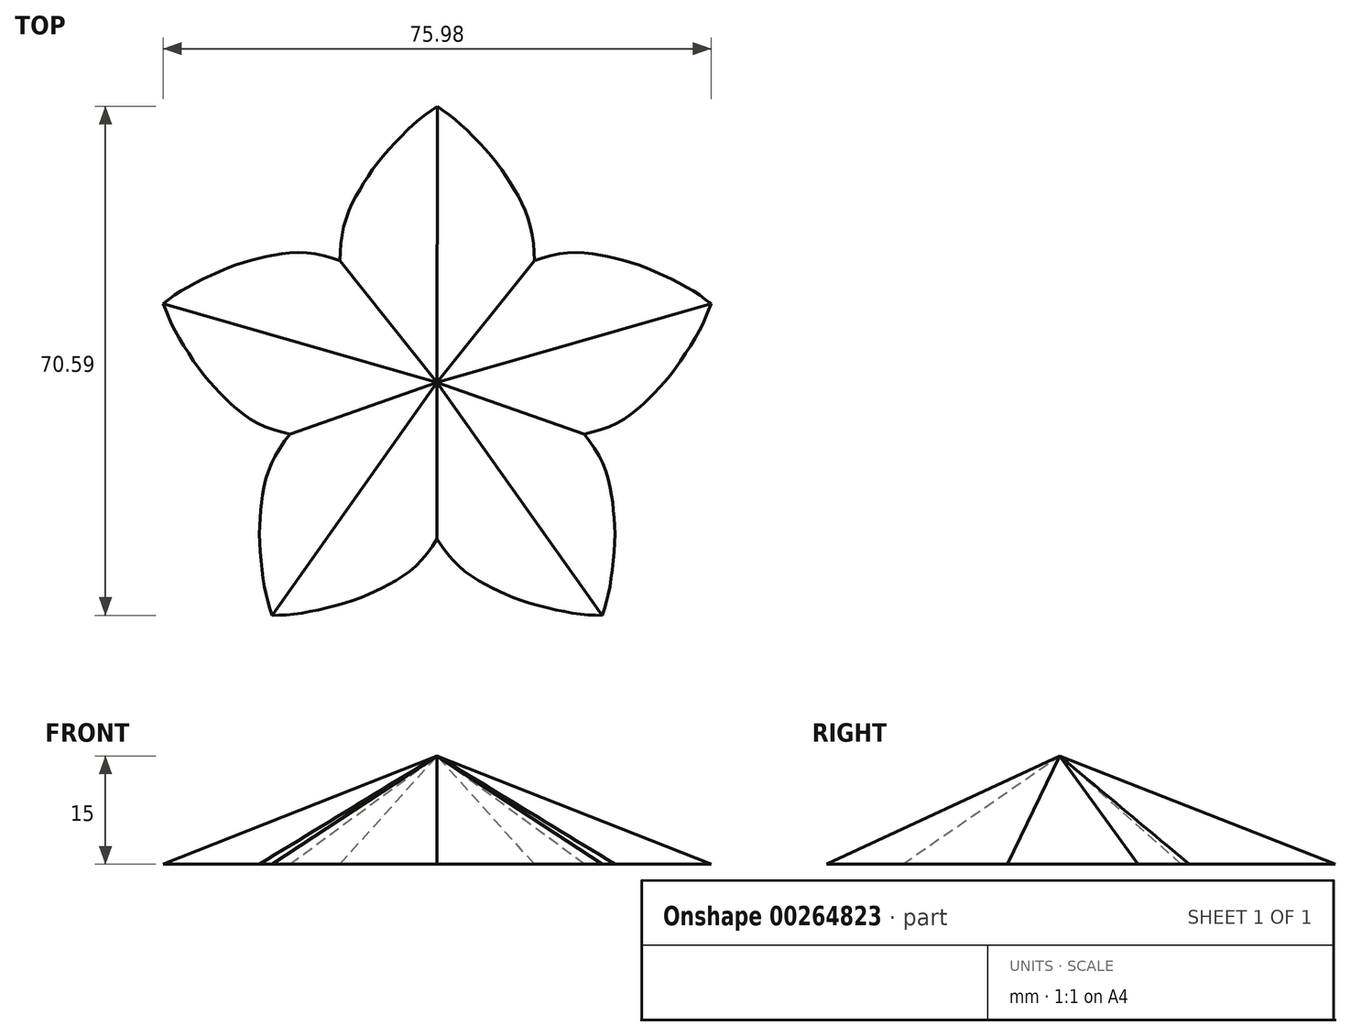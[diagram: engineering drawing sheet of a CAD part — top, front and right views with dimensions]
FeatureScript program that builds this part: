
annotation { "Feature Type Name" : "Feature", "Feature Type Description" : "" }
export const myFeature = defineFeature(function(context is Context, id is Id, definition is map)
    precondition{}
    {
        {
            var Q0;
            Q0=qCreatedBy(makeId("Top.planeOp"),FACE);
            var sketch = newSketch(context, id + "F0", { "sketchPlane" : qUnion([Q0])});
            skFitSpline(sketch, "E0", {"points": [v(-0.02, -18.8) * mm, v(2.46, -22.06) * mm, v(5.56, -24.49) * mm, v(8.5, -26.02) * mm, v(11.82, -27.4) * mm, v(16.13, -28.56) * mm, v(19.98, -29.26) * mm, v(22.9, -29.4) * mm], "startDerivative": vector(15.3, -22.9) * mm, "endDerivative": vector(22.31, -0.58) * mm});
            skFitSpline(sketch, "E1.MirrorCS", {"points": [v(0, -18.8) * mm, v(-2.46, -22.06) * mm, v(-5.56, -24.49) * mm, v(-8.5, -26.02) * mm, v(-11.82, -27.4) * mm, v(-16.13, -28.56) * mm, v(-19.98, -29.26) * mm, v(-22.9, -29.4) * mm], "startDerivative": vector(-15.3, -22.9) * mm, "endDerivative": vector(-22.31, -0.58) * mm});
            skFitSpline(sketch, "E2.MirrorCS", {"points": [v(-20.43, -4.3) * mm, v(-22.7, -7.7) * mm, v(-23.96, -11.42) * mm, v(-24.44, -14.7) * mm, v(-24.64, -18.3) * mm, v(-24.32, -22.75) * mm, v(-23.71, -26.6) * mm, v(-22.9, -29.4) * mm], "startDerivative": vector(-16.57, -22) * mm, "endDerivative": vector(6.8, -21.26) * mm});
            skFitSpline(sketch, "E3.MirrorCS", {"points": [v(20.43, -4.3) * mm, v(22.7, -7.7) * mm, v(23.96, -11.42) * mm, v(24.44, -14.7) * mm, v(24.64, -18.3) * mm, v(24.32, -22.75) * mm, v(23.71, -26.6) * mm, v(22.9, -29.4) * mm], "startDerivative": vector(16.57, -22) * mm, "endDerivative": vector(-6.8, -21.26) * mm});
            skFitSpline(sketch, "E4.MirrorCS", {"points": [v(-20.43, -4.3) * mm, v(-24.31, -3.05) * mm, v(-27.63, -0.92) * mm, v(-30.05, 1.35) * mm, v(-32.44, 4.03) * mm, v(-34.96, 7.72) * mm, v(-36.88, 11.12) * mm, v(-37.99, 13.82) * mm], "startDerivative": vector(-26.66, 6.9) * mm, "endDerivative": vector(-7.9, 20.87) * mm});
            skFitSpline(sketch, "E5.MirrorCS", {"points": [v(-13.48, 19.78) * mm, v(-17.42, 20.79) * mm, v(-21.36, 20.76) * mm, v(-24.62, 20.12) * mm, v(-28.07, 19.14) * mm, v(-32.17, 17.36) * mm, v(-35.61, 15.51) * mm, v(-37.99, 13.82) * mm], "startDerivative": vector(-26.23, 8.4) * mm, "endDerivative": vector(-17.83, -13.43) * mm});
            skFitSpline(sketch, "E6.MirrorCS", {"points": [v(20.43, -4.3) * mm, v(24.31, -3.05) * mm, v(27.63, -0.92) * mm, v(30.05, 1.35) * mm, v(32.44, 4.03) * mm, v(34.96, 7.72) * mm, v(36.88, 11.12) * mm, v(37.99, 13.82) * mm], "startDerivative": vector(26.66, 6.9) * mm, "endDerivative": vector(7.9, 20.87) * mm});
            skFitSpline(sketch, "E7.MirrorCS", {"points": [v(-13.48, 19.78) * mm, v(-13.1, 23.87) * mm, v(-11.83, 27.6) * mm, v(-10.2, 30.49) * mm, v(-8.18, 33.45) * mm, v(-5.2, 36.79) * mm, v(-2.37, 39.47) * mm, v(0.04, 41.2) * mm], "startDerivative": vector(0.3, 27.54) * mm, "endDerivative": vector(18.36, 12.69) * mm});
            skFitSpline(sketch, "E8.MirrorCS", {"points": [v(13.48, 19.78) * mm, v(17.42, 20.79) * mm, v(21.36, 20.76) * mm, v(24.62, 20.12) * mm, v(28.07, 19.14) * mm, v(32.17, 17.36) * mm, v(35.61, 15.51) * mm, v(37.99, 13.82) * mm], "startDerivative": vector(26.23, 8.4) * mm, "endDerivative": vector(17.83, -13.43) * mm});
            skFitSpline(sketch, "E9.MirrorCS", {"points": [v(13.48, 19.78) * mm, v(13.1, 23.87) * mm, v(11.83, 27.6) * mm, v(10.2, 30.49) * mm, v(8.18, 33.45) * mm, v(5.2, 36.79) * mm, v(2.37, 39.47) * mm, v(0, 41.2) * mm], "startDerivative": vector(-0.3, 27.54) * mm, "endDerivative": vector(-18.36, 12.69) * mm});
            skLineSegment(sketch, "E10", {"start": v(0.04, 41.2) * mm, "end": v(-0.02, -18.8) * mm, "construction": true});
            skPoint(sketch, "E11.0.midPoint", {"position": v(0.01, 17.8) * mm});
            skSolve(sketch);
        }
        {
            var Q0;
            Q0=qCreatedBy(makeId("Top.planeOp"),FACE);
            cPlane(context, id + "F1", {"entities" : qUnion([Q0]), "cplaneType" : CPlaneType.OFFSET, "offset" : 15 * mm, "width" : 150 * mm, "height" : 150 * mm});
        }
        {
            var Q0;
            Q0=qCreatedBy(id+"F1.planeOp",FACE);
            var sketch = newSketch(context, id + "F2", { "sketchPlane" : qUnion([Q0])});
            skPoint(sketch, "E12", {"position": v(0, 2.92) * mm});
            skSolve(sketch);
        }
        {
            var Q0;
            {var subQ1=sQuery(id+"F0.wireOp",EDGE,"E2.MirrorCS");Q0=makeQuery(id+"F0.imprint","IMPRINT",FACE,{"disambiguationData":[TD([[makeQuery(id+"F0.imprint","IMPRINT",EDGE,{"derivedFrom":subQ1}),1.0]])]});}
            var Q1;
            Q1=sQuery(id+"F2.wireOp",VERTEX,"E12");
            loft(context, id + "F3", {"sheetProfilesArray" : [{ "sheetProfileEntities" : qUnion([Q0]) }, { "sheetProfileEntities" : qUnion([Q1]) }]});
        }
    });
